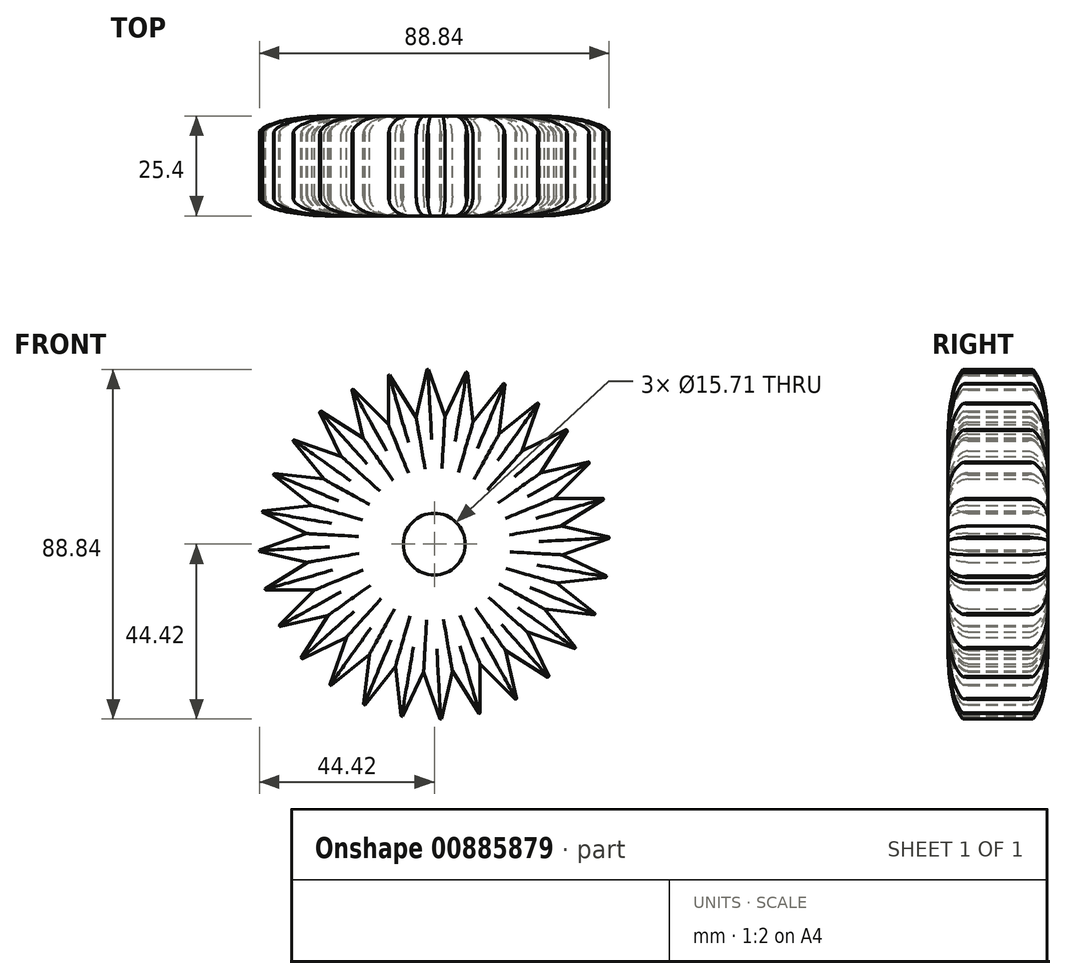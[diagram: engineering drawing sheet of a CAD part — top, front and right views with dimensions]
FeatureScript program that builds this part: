
annotation { "Feature Type Name" : "Feature", "Feature Type Description" : "" }
export const myFeature = defineFeature(function(context is Context, id is Id, definition is map)
    precondition{}
    {
        {
            var Q0;
            Q0=qCreatedBy(makeId("Front.planeOp"),FACE);
            var sketch = newSketch(context, id + "F0", { "sketchPlane" : qUnion([Q0])});
            skArc(sketch, "E0", {"start": v(33.8, 28.87) * mm, "mid": v(33.7, 28.98) * mm, "end": v(33.6, 29.1) * mm});
            skLineSegment(sketch, "E1", {"start": v(-20.62, 39.38) * mm, "end": v(-11.64, 30.4) * mm});
            skLineSegment(sketch, "E2", {"start": v(-11.64, 30.4) * mm, "end": v(-11.64, 42.9) * mm});
            skLineSegment(sketch, "E3.1.0", {"start": v(-28.87, 33.8) * mm, "end": v(-18.11, 27.04) * mm});
            skLineSegment(sketch, "E3.2.0", {"start": v(-35.66, 26.53) * mm, "end": v(-23.68, 22.34) * mm});
            skLineSegment(sketch, "E4.1.3.0", {"start": v(-40.67, 17.93) * mm, "end": v(-28.05, 16.5) * mm});
            skLineSegment(sketch, "E4.1.4.0", {"start": v(-43.64, 8.43) * mm, "end": v(-31.02, 9.85) * mm});
            skLineSegment(sketch, "E4.1.5.0", {"start": v(-44.42, -1.5) * mm, "end": v(-32.44, 2.7) * mm});
            skLineSegment(sketch, "E4.1.6.0", {"start": v(-42.98, -11.34) * mm, "end": v(-32.23, -4.59) * mm});
            skLineSegment(sketch, "E4.1.7.0", {"start": v(-39.38, -20.62) * mm, "end": v(-30.4, -11.64) * mm});
            skLineSegment(sketch, "E4.1.8.0", {"start": v(-33.8, -28.87) * mm, "end": v(-27.04, -18.11) * mm});
            skLineSegment(sketch, "E4.1.9.0", {"start": v(-26.53, -35.66) * mm, "end": v(-22.34, -23.68) * mm});
            skLineSegment(sketch, "E4.1.10.0", {"start": v(-17.93, -40.67) * mm, "end": v(-16.5, -28.05) * mm});
            skLineSegment(sketch, "E4.1.11.0", {"start": v(-8.43, -43.64) * mm, "end": v(-9.85, -31.02) * mm});
            skLineSegment(sketch, "E5.1.0", {"start": v(-18.11, 27.04) * mm, "end": v(-20.9, 39.23) * mm});
            skLineSegment(sketch, "E5.2.0", {"start": v(-23.68, 22.34) * mm, "end": v(-29.1, 33.6) * mm});
            skLineSegment(sketch, "E5.3.0", {"start": v(-28.05, 16.5) * mm, "end": v(-35.85, 26.28) * mm});
            skLineSegment(sketch, "E5.4.0", {"start": v(-31.02, 9.85) * mm, "end": v(-40.8, 17.64) * mm});
            skLineSegment(sketch, "E5.5.0", {"start": v(-32.44, 2.7) * mm, "end": v(-43.7, 8.12) * mm});
            skLineSegment(sketch, "E5.6.0", {"start": v(-32.23, -4.59) * mm, "end": v(-44.41, -1.8) * mm});
            skLineSegment(sketch, "E5.7.0", {"start": v(-30.4, -11.64) * mm, "end": v(-42.9, -11.64) * mm});
            skLineSegment(sketch, "E5.8.0", {"start": v(-27.04, -18.11) * mm, "end": v(-39.23, -20.9) * mm});
            skLineSegment(sketch, "E5.9.0", {"start": v(-22.34, -23.68) * mm, "end": v(-33.6, -29.1) * mm});
            skLineSegment(sketch, "E5.10.0", {"start": v(-16.5, -28.05) * mm, "end": v(-26.28, -35.85) * mm});
            skLineSegment(sketch, "E5.11.0", {"start": v(-9.85, -31.02) * mm, "end": v(-17.64, -40.8) * mm});
            skLineSegment(sketch, "E6.1.12.0", {"start": v(-2.7, -32.44) * mm, "end": v(-8.12, -43.7) * mm});
            skLineSegment(sketch, "E6.1.13.0", {"start": v(4.59, -32.23) * mm, "end": v(1.8, -44.41) * mm});
            skLineSegment(sketch, "E6.1.14.0", {"start": v(11.64, -30.4) * mm, "end": v(11.64, -42.9) * mm});
            skLineSegment(sketch, "E7.1.12.0", {"start": v(1.5, -44.42) * mm, "end": v(-2.7, -32.44) * mm});
            skLineSegment(sketch, "E7.1.13.0", {"start": v(11.34, -42.98) * mm, "end": v(4.59, -32.23) * mm});
            skLineSegment(sketch, "E7.1.14.0", {"start": v(20.62, -39.38) * mm, "end": v(11.64, -30.4) * mm});
            skLineSegment(sketch, "E8.1.15.0", {"start": v(28.87, -33.8) * mm, "end": v(18.11, -27.04) * mm});
            skLineSegment(sketch, "E9.1.15.0", {"start": v(18.11, -27.04) * mm, "end": v(20.9, -39.23) * mm});
            skLineSegment(sketch, "E10.1.16.0", {"start": v(35.66, -26.53) * mm, "end": v(23.68, -22.34) * mm});
            skLineSegment(sketch, "E10.1.17.0", {"start": v(40.67, -17.93) * mm, "end": v(28.05, -16.5) * mm});
            skLineSegment(sketch, "E10.1.18.0", {"start": v(43.64, -8.43) * mm, "end": v(31.02, -9.85) * mm});
            skLineSegment(sketch, "E10.1.19.0", {"start": v(44.42, 1.5) * mm, "end": v(32.44, -2.7) * mm});
            skLineSegment(sketch, "E11.1.16.0", {"start": v(23.68, -22.34) * mm, "end": v(29.1, -33.6) * mm});
            skLineSegment(sketch, "E11.1.17.0", {"start": v(28.05, -16.5) * mm, "end": v(35.85, -26.28) * mm});
            skLineSegment(sketch, "E11.1.18.0", {"start": v(31.02, -9.85) * mm, "end": v(40.8, -17.64) * mm});
            skLineSegment(sketch, "E11.1.19.0", {"start": v(32.44, -2.7) * mm, "end": v(43.7, -8.12) * mm});
            skLineSegment(sketch, "E12.1.20.0", {"start": v(42.98, 11.34) * mm, "end": v(32.23, 4.59) * mm});
            skLineSegment(sketch, "E12.1.21.0", {"start": v(39.38, 20.62) * mm, "end": v(30.4, 11.64) * mm});
            skLineSegment(sketch, "E12.1.22.0", {"start": v(33.8, 28.87) * mm, "end": v(27.04, 18.11) * mm});
            skLineSegment(sketch, "E12.1.23.0", {"start": v(26.53, 35.66) * mm, "end": v(22.34, 23.68) * mm});
            skLineSegment(sketch, "E12.1.24.0", {"start": v(17.93, 40.67) * mm, "end": v(16.5, 28.05) * mm});
            skLineSegment(sketch, "E13.1.20.0", {"start": v(32.23, 4.59) * mm, "end": v(44.41, 1.8) * mm});
            skLineSegment(sketch, "E13.1.21.0", {"start": v(30.4, 11.64) * mm, "end": v(42.9, 11.64) * mm});
            skLineSegment(sketch, "E13.1.22.0", {"start": v(27.04, 18.11) * mm, "end": v(39.23, 20.9) * mm});
            skLineSegment(sketch, "E13.1.23.0", {"start": v(22.34, 23.68) * mm, "end": v(33.6, 29.1) * mm});
            skLineSegment(sketch, "E13.1.24.0", {"start": v(16.5, 28.05) * mm, "end": v(26.28, 35.85) * mm});
            skLineSegment(sketch, "E14.1.25.0", {"start": v(9.85, 31.02) * mm, "end": v(17.64, 40.8) * mm});
            skLineSegment(sketch, "E15.1.25.0", {"start": v(8.43, 43.64) * mm, "end": v(9.85, 31.02) * mm});
            skLineSegment(sketch, "E16.1.26.0", {"start": v(-1.5, 44.42) * mm, "end": v(2.7, 32.44) * mm});
            skLineSegment(sketch, "E16.1.27.0", {"start": v(-11.34, 42.98) * mm, "end": v(-4.59, 32.23) * mm});
            skLineSegment(sketch, "E17.1.26.0", {"start": v(2.7, 32.44) * mm, "end": v(8.12, 43.7) * mm});
            skLineSegment(sketch, "E17.1.27.0", {"start": v(-4.59, 32.23) * mm, "end": v(-1.8, 44.41) * mm});
            skArc(sketch, "E18.trimOffspring", {"start": v(39.38, 20.62) * mm, "mid": v(39.3, 20.76) * mm, "end": v(39.23, 20.9) * mm});
            skArc(sketch, "E19.trimOffspring", {"start": v(42.98, 11.34) * mm, "mid": v(42.94, 11.5) * mm, "end": v(42.9, 11.64) * mm});
            skArc(sketch, "E20.trimOffspring", {"start": v(44.42, 1.5) * mm, "mid": v(44.42, 1.65) * mm, "end": v(44.41, 1.8) * mm});
            skArc(sketch, "E21.trimOffspring", {"start": v(43.64, -8.43) * mm, "mid": v(43.67, -8.28) * mm, "end": v(43.7, -8.12) * mm});
            skArc(sketch, "E22.trimOffspring", {"start": v(40.67, -17.93) * mm, "mid": v(40.74, -17.79) * mm, "end": v(40.8, -17.64) * mm});
            skArc(sketch, "E23.trimOffspring", {"start": v(35.66, -26.53) * mm, "mid": v(35.76, -26.4) * mm, "end": v(35.85, -26.28) * mm});
            skArc(sketch, "E24.trimOffspring", {"start": v(28.87, -33.8) * mm, "mid": v(28.98, -33.7) * mm, "end": v(29.1, -33.6) * mm});
            skArc(sketch, "E25.trimOffspring", {"start": v(20.62, -39.38) * mm, "mid": v(20.76, -39.3) * mm, "end": v(20.9, -39.23) * mm});
            skArc(sketch, "E26.trimOffspring", {"start": v(11.34, -42.98) * mm, "mid": v(11.5, -42.94) * mm, "end": v(11.64, -42.9) * mm});
            skArc(sketch, "E27.trimOffspring", {"start": v(1.5, -44.42) * mm, "mid": v(1.65, -44.42) * mm, "end": v(1.8, -44.41) * mm});
            skArc(sketch, "E28.trimOffspring", {"start": v(-8.43, -43.64) * mm, "mid": v(-8.28, -43.67) * mm, "end": v(-8.12, -43.7) * mm});
            skArc(sketch, "E29.trimOffspring", {"start": v(-17.93, -40.67) * mm, "mid": v(-17.79, -40.74) * mm, "end": v(-17.64, -40.8) * mm});
            skArc(sketch, "E30.trimOffspring", {"start": v(-26.53, -35.66) * mm, "mid": v(-26.4, -35.76) * mm, "end": v(-26.28, -35.85) * mm});
            skArc(sketch, "E31.trimOffspring", {"start": v(26.53, 35.66) * mm, "mid": v(26.4, 35.76) * mm, "end": v(26.28, 35.85) * mm});
            skArc(sketch, "E32.trimOffspring", {"start": v(17.93, 40.67) * mm, "mid": v(17.79, 40.74) * mm, "end": v(17.64, 40.8) * mm});
            skArc(sketch, "E33.trimOffspring", {"start": v(8.43, 43.64) * mm, "mid": v(8.28, 43.67) * mm, "end": v(8.12, 43.7) * mm});
            skArc(sketch, "E34.trimOffspring", {"start": v(-1.5, 44.42) * mm, "mid": v(-1.65, 44.42) * mm, "end": v(-1.8, 44.41) * mm});
            skArc(sketch, "E35.trimOffspring", {"start": v(-11.34, 42.98) * mm, "mid": v(-11.5, 42.94) * mm, "end": v(-11.64, 42.9) * mm});
            skArc(sketch, "E36.trimOffspring", {"start": v(-20.62, 39.38) * mm, "mid": v(-20.76, 39.3) * mm, "end": v(-20.9, 39.23) * mm});
            skArc(sketch, "E37.trimOffspring", {"start": v(-28.87, 33.8) * mm, "mid": v(-28.98, 33.7) * mm, "end": v(-29.1, 33.6) * mm});
            skArc(sketch, "E38.trimOffspring", {"start": v(-33.8, -28.87) * mm, "mid": v(-33.7, -28.98) * mm, "end": v(-33.6, -29.1) * mm});
            skArc(sketch, "E39.trimOffspring", {"start": v(-39.38, -20.62) * mm, "mid": v(-39.3, -20.76) * mm, "end": v(-39.23, -20.9) * mm});
            skArc(sketch, "E40.trimOffspring", {"start": v(-42.98, -11.34) * mm, "mid": v(-42.94, -11.5) * mm, "end": v(-42.9, -11.64) * mm});
            skArc(sketch, "E41.trimOffspring", {"start": v(-44.42, -1.5) * mm, "mid": v(-44.42, -1.65) * mm, "end": v(-44.41, -1.8) * mm});
            skArc(sketch, "E42.trimOffspring", {"start": v(-43.64, 8.43) * mm, "mid": v(-43.67, 8.28) * mm, "end": v(-43.7, 8.12) * mm});
            skArc(sketch, "E43.trimOffspring", {"start": v(-40.67, 17.93) * mm, "mid": v(-40.74, 17.79) * mm, "end": v(-40.8, 17.64) * mm});
            skArc(sketch, "E44.trimOffspring", {"start": v(-35.66, 26.53) * mm, "mid": v(-35.76, 26.4) * mm, "end": v(-35.85, 26.28) * mm});
            skCircle(sketch, "E45", {"center": v(0, 0) * mm, "radius": 7.86 * mm});
            skSolve(sketch);
        }
        {
            var Q0;
            Q0 = qSketchRegion(id + "F0", true);
            extrude(context, id + "F1", {"entities" : qUnion([Q0]), "depth" : 25.4 * mm, "offsetDistance" : 25.4 * mm});
        }
        {
            var Q0;
            Q0=makeQuery(id+"F1.opExtrude","CAP_FACE",FACE,{"disambiguationData":[OSD([sQuery(id+"F0.wireOp",EDGE,"E0"),sQuery(id+"F0.wireOp",EDGE,"E1"),sQuery(id+"F0.wireOp",EDGE,"E2"),sQuery(id+"F0.wireOp",EDGE,"E3.1.0"),sQuery(id+"F0.wireOp",EDGE,"E3.2.0"),sQuery(id+"F0.wireOp",EDGE,"E4.1.3.0"),sQuery(id+"F0.wireOp",EDGE,"E4.1.4.0"),sQuery(id+"F0.wireOp",EDGE,"E4.1.5.0"),sQuery(id+"F0.wireOp",EDGE,"E4.1.6.0"),sQuery(id+"F0.wireOp",EDGE,"E4.1.7.0"),sQuery(id+"F0.wireOp",EDGE,"E4.1.8.0"),sQuery(id+"F0.wireOp",EDGE,"E4.1.9.0"),sQuery(id+"F0.wireOp",EDGE,"E4.1.10.0"),sQuery(id+"F0.wireOp",EDGE,"E4.1.11.0"),sQuery(id+"F0.wireOp",EDGE,"E5.1.0"),sQuery(id+"F0.wireOp",EDGE,"E5.2.0"),sQuery(id+"F0.wireOp",EDGE,"E5.3.0"),sQuery(id+"F0.wireOp",EDGE,"E5.4.0"),sQuery(id+"F0.wireOp",EDGE,"E5.5.0"),sQuery(id+"F0.wireOp",EDGE,"E5.6.0"),sQuery(id+"F0.wireOp",EDGE,"E5.7.0"),sQuery(id+"F0.wireOp",EDGE,"E5.8.0"),sQuery(id+"F0.wireOp",EDGE,"E5.9.0"),sQuery(id+"F0.wireOp",EDGE,"E5.10.0"),sQuery(id+"F0.wireOp",EDGE,"E5.11.0"),sQuery(id+"F0.wireOp",EDGE,"E6.1.12.0"),sQuery(id+"F0.wireOp",EDGE,"E6.1.13.0"),sQuery(id+"F0.wireOp",EDGE,"E6.1.14.0"),sQuery(id+"F0.wireOp",EDGE,"E7.1.12.0"),sQuery(id+"F0.wireOp",EDGE,"E7.1.13.0"),sQuery(id+"F0.wireOp",EDGE,"E7.1.14.0"),sQuery(id+"F0.wireOp",EDGE,"E8.1.15.0"),sQuery(id+"F0.wireOp",EDGE,"E9.1.15.0"),sQuery(id+"F0.wireOp",EDGE,"E10.1.16.0"),sQuery(id+"F0.wireOp",EDGE,"E10.1.17.0"),sQuery(id+"F0.wireOp",EDGE,"E10.1.18.0"),sQuery(id+"F0.wireOp",EDGE,"E10.1.19.0"),sQuery(id+"F0.wireOp",EDGE,"E11.1.16.0"),sQuery(id+"F0.wireOp",EDGE,"E11.1.17.0"),sQuery(id+"F0.wireOp",EDGE,"E11.1.18.0"),sQuery(id+"F0.wireOp",EDGE,"E11.1.19.0"),sQuery(id+"F0.wireOp",EDGE,"E12.1.20.0"),sQuery(id+"F0.wireOp",EDGE,"E12.1.21.0"),sQuery(id+"F0.wireOp",EDGE,"E12.1.22.0"),sQuery(id+"F0.wireOp",EDGE,"E12.1.23.0"),sQuery(id+"F0.wireOp",EDGE,"E12.1.24.0"),sQuery(id+"F0.wireOp",EDGE,"E13.1.20.0"),sQuery(id+"F0.wireOp",EDGE,"E13.1.21.0"),sQuery(id+"F0.wireOp",EDGE,"E13.1.22.0"),sQuery(id+"F0.wireOp",EDGE,"E13.1.23.0"),sQuery(id+"F0.wireOp",EDGE,"E13.1.24.0"),sQuery(id+"F0.wireOp",EDGE,"E14.1.25.0"),sQuery(id+"F0.wireOp",EDGE,"E15.1.25.0"),sQuery(id+"F0.wireOp",EDGE,"E16.1.26.0"),sQuery(id+"F0.wireOp",EDGE,"E16.1.27.0"),sQuery(id+"F0.wireOp",EDGE,"E17.1.26.0"),sQuery(id+"F0.wireOp",EDGE,"E17.1.27.0"),sQuery(id+"F0.wireOp",EDGE,"E18.trimOffspring"),sQuery(id+"F0.wireOp",EDGE,"E19.trimOffspring"),sQuery(id+"F0.wireOp",EDGE,"E20.trimOffspring"),sQuery(id+"F0.wireOp",EDGE,"E21.trimOffspring"),sQuery(id+"F0.wireOp",EDGE,"E22.trimOffspring"),sQuery(id+"F0.wireOp",EDGE,"E23.trimOffspring"),sQuery(id+"F0.wireOp",EDGE,"E24.trimOffspring"),sQuery(id+"F0.wireOp",EDGE,"E25.trimOffspring"),sQuery(id+"F0.wireOp",EDGE,"E26.trimOffspring"),sQuery(id+"F0.wireOp",EDGE,"E27.trimOffspring"),sQuery(id+"F0.wireOp",EDGE,"E28.trimOffspring"),sQuery(id+"F0.wireOp",EDGE,"E29.trimOffspring"),sQuery(id+"F0.wireOp",EDGE,"E30.trimOffspring"),sQuery(id+"F0.wireOp",EDGE,"E31.trimOffspring"),sQuery(id+"F0.wireOp",EDGE,"E32.trimOffspring"),sQuery(id+"F0.wireOp",EDGE,"E33.trimOffspring"),sQuery(id+"F0.wireOp",EDGE,"E34.trimOffspring"),sQuery(id+"F0.wireOp",EDGE,"E35.trimOffspring"),sQuery(id+"F0.wireOp",EDGE,"E36.trimOffspring"),sQuery(id+"F0.wireOp",EDGE,"E37.trimOffspring"),sQuery(id+"F0.wireOp",EDGE,"E38.trimOffspring"),sQuery(id+"F0.wireOp",EDGE,"E39.trimOffspring"),sQuery(id+"F0.wireOp",EDGE,"E40.trimOffspring"),sQuery(id+"F0.wireOp",EDGE,"E41.trimOffspring"),sQuery(id+"F0.wireOp",EDGE,"E42.trimOffspring"),sQuery(id+"F0.wireOp",EDGE,"E43.trimOffspring"),sQuery(id+"F0.wireOp",EDGE,"E44.trimOffspring"),sQuery(id+"F0.wireOp",EDGE,"E45")])],"isStart":true});
            var Q1;
            Q1=makeQuery(id+"F1.opExtrude","CAP_FACE",FACE,{"disambiguationData":[OSD([sQuery(id+"F0.wireOp",EDGE,"E0"),sQuery(id+"F0.wireOp",EDGE,"E1"),sQuery(id+"F0.wireOp",EDGE,"E2"),sQuery(id+"F0.wireOp",EDGE,"E3.1.0"),sQuery(id+"F0.wireOp",EDGE,"E3.2.0"),sQuery(id+"F0.wireOp",EDGE,"E4.1.3.0"),sQuery(id+"F0.wireOp",EDGE,"E4.1.4.0"),sQuery(id+"F0.wireOp",EDGE,"E4.1.5.0"),sQuery(id+"F0.wireOp",EDGE,"E4.1.6.0"),sQuery(id+"F0.wireOp",EDGE,"E4.1.7.0"),sQuery(id+"F0.wireOp",EDGE,"E4.1.8.0"),sQuery(id+"F0.wireOp",EDGE,"E4.1.9.0"),sQuery(id+"F0.wireOp",EDGE,"E4.1.10.0"),sQuery(id+"F0.wireOp",EDGE,"E4.1.11.0"),sQuery(id+"F0.wireOp",EDGE,"E5.1.0"),sQuery(id+"F0.wireOp",EDGE,"E5.2.0"),sQuery(id+"F0.wireOp",EDGE,"E5.3.0"),sQuery(id+"F0.wireOp",EDGE,"E5.4.0"),sQuery(id+"F0.wireOp",EDGE,"E5.5.0"),sQuery(id+"F0.wireOp",EDGE,"E5.6.0"),sQuery(id+"F0.wireOp",EDGE,"E5.7.0"),sQuery(id+"F0.wireOp",EDGE,"E5.8.0"),sQuery(id+"F0.wireOp",EDGE,"E5.9.0"),sQuery(id+"F0.wireOp",EDGE,"E5.10.0"),sQuery(id+"F0.wireOp",EDGE,"E5.11.0"),sQuery(id+"F0.wireOp",EDGE,"E6.1.12.0"),sQuery(id+"F0.wireOp",EDGE,"E6.1.13.0"),sQuery(id+"F0.wireOp",EDGE,"E6.1.14.0"),sQuery(id+"F0.wireOp",EDGE,"E7.1.12.0"),sQuery(id+"F0.wireOp",EDGE,"E7.1.13.0"),sQuery(id+"F0.wireOp",EDGE,"E7.1.14.0"),sQuery(id+"F0.wireOp",EDGE,"E8.1.15.0"),sQuery(id+"F0.wireOp",EDGE,"E9.1.15.0"),sQuery(id+"F0.wireOp",EDGE,"E10.1.16.0"),sQuery(id+"F0.wireOp",EDGE,"E10.1.17.0"),sQuery(id+"F0.wireOp",EDGE,"E10.1.18.0"),sQuery(id+"F0.wireOp",EDGE,"E10.1.19.0"),sQuery(id+"F0.wireOp",EDGE,"E11.1.16.0"),sQuery(id+"F0.wireOp",EDGE,"E11.1.17.0"),sQuery(id+"F0.wireOp",EDGE,"E11.1.18.0"),sQuery(id+"F0.wireOp",EDGE,"E11.1.19.0"),sQuery(id+"F0.wireOp",EDGE,"E12.1.20.0"),sQuery(id+"F0.wireOp",EDGE,"E12.1.21.0"),sQuery(id+"F0.wireOp",EDGE,"E12.1.22.0"),sQuery(id+"F0.wireOp",EDGE,"E12.1.23.0"),sQuery(id+"F0.wireOp",EDGE,"E12.1.24.0"),sQuery(id+"F0.wireOp",EDGE,"E13.1.20.0"),sQuery(id+"F0.wireOp",EDGE,"E13.1.21.0"),sQuery(id+"F0.wireOp",EDGE,"E13.1.22.0"),sQuery(id+"F0.wireOp",EDGE,"E13.1.23.0"),sQuery(id+"F0.wireOp",EDGE,"E13.1.24.0"),sQuery(id+"F0.wireOp",EDGE,"E14.1.25.0"),sQuery(id+"F0.wireOp",EDGE,"E15.1.25.0"),sQuery(id+"F0.wireOp",EDGE,"E16.1.26.0"),sQuery(id+"F0.wireOp",EDGE,"E16.1.27.0"),sQuery(id+"F0.wireOp",EDGE,"E17.1.26.0"),sQuery(id+"F0.wireOp",EDGE,"E17.1.27.0"),sQuery(id+"F0.wireOp",EDGE,"E18.trimOffspring"),sQuery(id+"F0.wireOp",EDGE,"E19.trimOffspring"),sQuery(id+"F0.wireOp",EDGE,"E20.trimOffspring"),sQuery(id+"F0.wireOp",EDGE,"E21.trimOffspring"),sQuery(id+"F0.wireOp",EDGE,"E22.trimOffspring"),sQuery(id+"F0.wireOp",EDGE,"E23.trimOffspring"),sQuery(id+"F0.wireOp",EDGE,"E24.trimOffspring"),sQuery(id+"F0.wireOp",EDGE,"E25.trimOffspring"),sQuery(id+"F0.wireOp",EDGE,"E26.trimOffspring"),sQuery(id+"F0.wireOp",EDGE,"E27.trimOffspring"),sQuery(id+"F0.wireOp",EDGE,"E28.trimOffspring"),sQuery(id+"F0.wireOp",EDGE,"E29.trimOffspring"),sQuery(id+"F0.wireOp",EDGE,"E30.trimOffspring"),sQuery(id+"F0.wireOp",EDGE,"E31.trimOffspring"),sQuery(id+"F0.wireOp",EDGE,"E32.trimOffspring"),sQuery(id+"F0.wireOp",EDGE,"E33.trimOffspring"),sQuery(id+"F0.wireOp",EDGE,"E34.trimOffspring"),sQuery(id+"F0.wireOp",EDGE,"E35.trimOffspring"),sQuery(id+"F0.wireOp",EDGE,"E36.trimOffspring"),sQuery(id+"F0.wireOp",EDGE,"E37.trimOffspring"),sQuery(id+"F0.wireOp",EDGE,"E38.trimOffspring"),sQuery(id+"F0.wireOp",EDGE,"E39.trimOffspring"),sQuery(id+"F0.wireOp",EDGE,"E40.trimOffspring"),sQuery(id+"F0.wireOp",EDGE,"E41.trimOffspring"),sQuery(id+"F0.wireOp",EDGE,"E42.trimOffspring"),sQuery(id+"F0.wireOp",EDGE,"E43.trimOffspring"),sQuery(id+"F0.wireOp",EDGE,"E44.trimOffspring"),sQuery(id+"F0.wireOp",EDGE,"E45")])],"isStart":false});
            fillet(context, id + "F2", {"entities" : qUnion([Q0, Q1]), "radius" : 5.08 * mm, "tangentPropagation" : true, "allowEdgeOverflow" : false});
        }
    });
